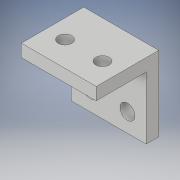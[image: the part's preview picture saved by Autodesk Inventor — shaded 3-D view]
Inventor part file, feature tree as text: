
AUTODESK INVENTOR PART (.ipt)
format: ipt  version: 2017 (Build 210142000, 142)  size: 125,952 bytes
history: native  units: in
note: dims shown in document units (in); Inventor stores cm internally (conversion verified against a paired STEP export)
features: sketch x3, hole x2, projected_geometry x2, extrude x1
ambient origin geometry x8: Origin, YZ Plane, XZ Plane, XY Plane, X Axis, Y Axis, Z Axis, Center Point
bodies: Solid1 (feature_tree)
feature tree (8):
  extrude  "Extrusion1"  Depth=0.625in
  hole  "Hole1"  [1 undecoded]
  hole  "Hole2"  [1 undecoded]
  sketch  "Sketch1"  dims[d0=0.75in d1=0.625in]
  sketch  "Sketch2"  dims[d2=0.625in d3=0.5in]
  projected_geometry  "Projected Loop1"
  sketch  "Sketch3"  dims[d4=0.75in d5=0.0in d6=0.375in d7=0.1875in d8=0.625in d11=0.135in d12=0.75in d13=0.375in d14=0.25in d15=0.5635in d16=1.0in d17=0.8108in d18=0.375in d19=0.375in d20=0.375in d21=0.1875in d22=0.1875in d23=0.1875in d24=0.15in d25=0.75in d26=0.375in d27=0.25in d28=0.5635in d29=1.0in d30=0.8108in d31=0.75in d32=0.75in]
  projected_geometry  "Projected Loop2"
note: 2 required parameter values undecoded (feature->parameter linkage not recoverable at this tier; creation-order binding heuristic only, values carry confidence <= 0.55)
